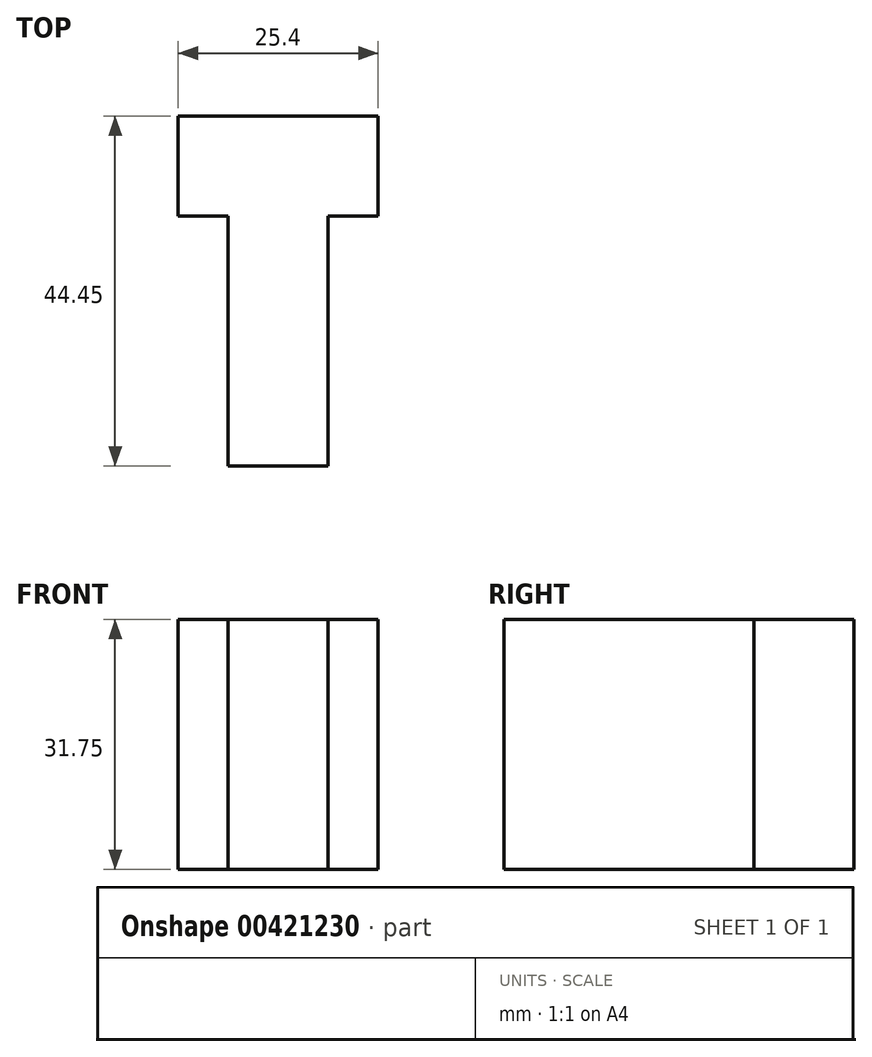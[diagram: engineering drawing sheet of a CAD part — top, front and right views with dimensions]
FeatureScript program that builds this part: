
annotation { "Feature Type Name" : "Feature", "Feature Type Description" : "" }
export const myFeature = defineFeature(function(context is Context, id is Id, definition is map)
    precondition{}
    {
        {
            var Q0;
            Q0=qCreatedBy(makeId("Top.planeOp"),FACE);
            var sketch = newSketch(context, id + "F0", { "sketchPlane" : qUnion([Q0])});
            skLineSegment(sketch, "E0", {"start": v(0, 0) * mm, "end": v(12.7, 0) * mm});
            skLineSegment(sketch, "E1", {"start": v(12.7, 0) * mm, "end": v(12.7, 31.75) * mm});
            skLineSegment(sketch, "E2", {"start": v(12.7, 31.75) * mm, "end": v(19.05, 31.75) * mm});
            skLineSegment(sketch, "E3", {"start": v(19.05, 31.75) * mm, "end": v(19.05, 44.45) * mm});
            skLineSegment(sketch, "E4", {"start": v(19.05, 44.45) * mm, "end": v(-6.35, 44.45) * mm});
            skLineSegment(sketch, "E5", {"start": v(-6.35, 44.45) * mm, "end": v(-6.35, 31.75) * mm});
            skLineSegment(sketch, "E6", {"start": v(-6.35, 31.75) * mm, "end": v(0, 31.75) * mm});
            skLineSegment(sketch, "E7", {"start": v(0, 31.75) * mm, "end": v(0, 0) * mm});
            skSolve(sketch);
        }
        {
            var Q0;
            Q0=makeQuery(id+"F0.imprint","IMPRINT",FACE,{"disambiguationData":[TD([[makeQuery(id+"F0.imprint","IMPRINT",EDGE,{"derivedFrom":sQuery(id+"F0.wireOp",EDGE,"E0")}),1.0]])]});
            extrude(context, id + "F1", {"entities" : qUnion([Q0]), "depth" : 31.75 * mm});
        }
    });
